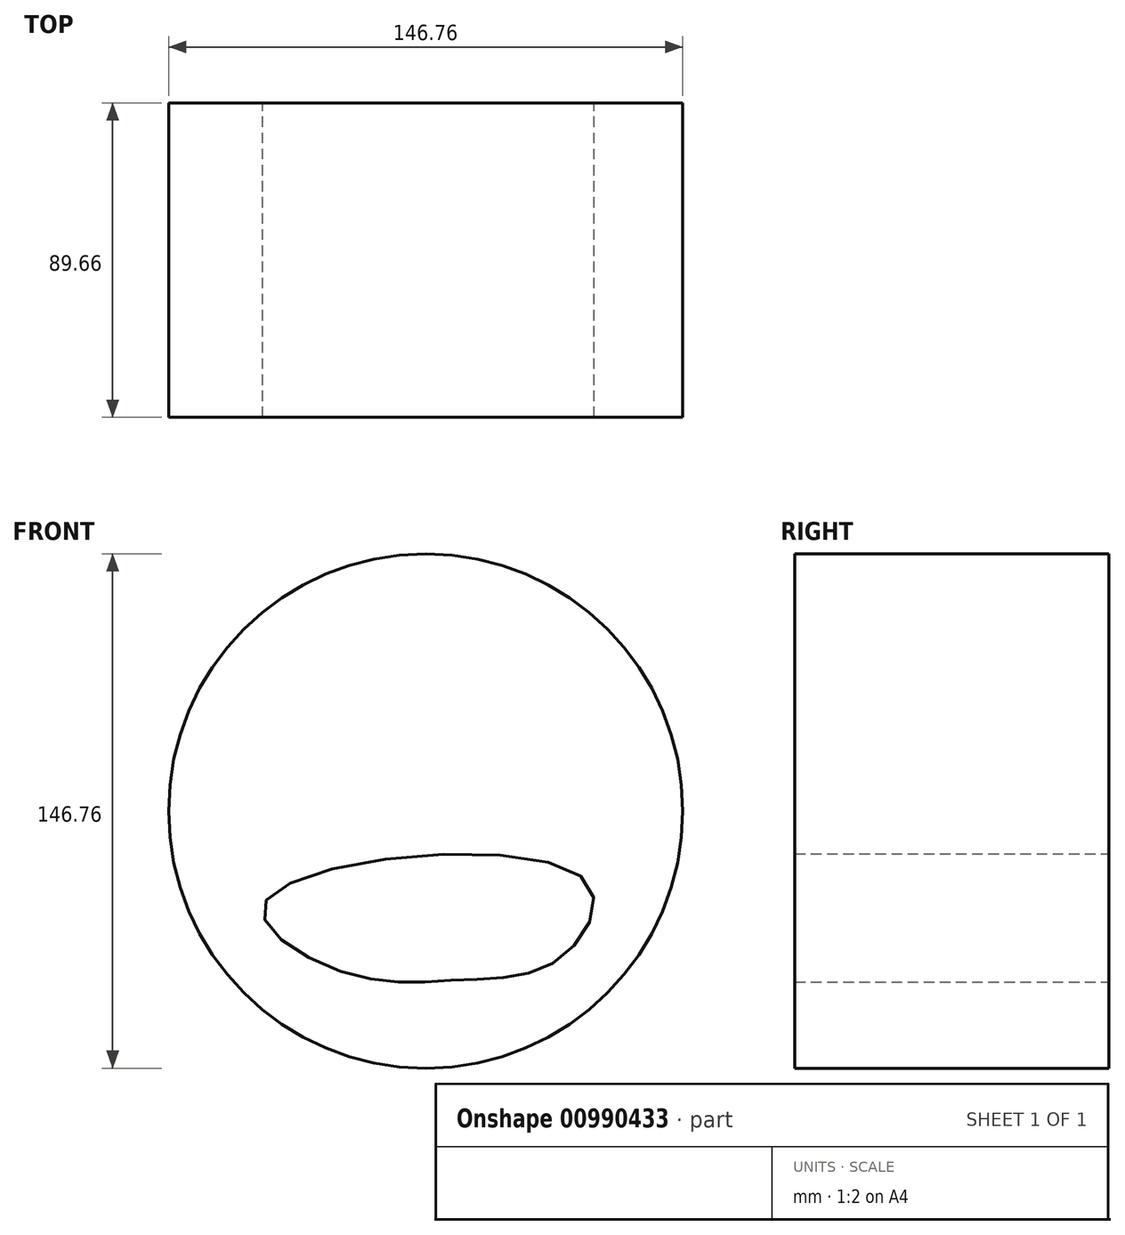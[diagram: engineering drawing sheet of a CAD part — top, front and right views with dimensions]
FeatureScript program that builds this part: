
annotation { "Feature Type Name" : "Feature", "Feature Type Description" : "" }
export const myFeature = defineFeature(function(context is Context, id is Id, definition is map)
    precondition{}
    {
        {
            var Q0;
            Q0=qCreatedBy(makeId("Front.planeOp"),FACE);
            var sketch = newSketch(context, id + "F0", { "sketchPlane" : qUnion([Q0])});
            skCircle(sketch, "E0", {"center": v(0, -1.7) * mm, "radius": 73.38 * mm});
            skSolve(sketch);
        }
        {
            var Q0;
            Q0=makeQuery(id+"F0.imprint","IMPRINT",FACE,{"disambiguationData":[TD([[makeQuery(id+"F0.imprint","IMPRINT",EDGE,{"derivedFrom":sQuery(id+"F0.wireOp",EDGE,"E0")}),1.0]])]});
            extrude(context, id + "F1", {"entities" : qUnion([Q0]), "depth" : 89.66 * mm, "offsetDistance" : 25.4 * mm});
        }
        {
            var Q0;
            Q0=makeQuery(id+"F1.opExtrude","CAP_FACE",FACE,{"disambiguationData":[OSD([sQuery(id+"F0.wireOp",EDGE,"E0")])],"isStart":false});
            var sketch = newSketch(context, id + "F2", { "sketchPlane" : qUnion([Q0])});
            skFitSpline(sketch, "E1", {"points": [v(-45.54, -27.2) * mm, v(-24.11, -47.54) * mm, v(9.65, -49.92) * mm, v(38.44, -43.64) * mm, v(44.5, -20.48) * mm, v(-45.54, -27.2) * mm]});
            skSolve(sketch);
        }
        {
            var Q0;
            Q0=makeQuery(id+"F2.imprint","IMPRINT",FACE,{"disambiguationData":[TD([[makeQuery(id+"F2.imprint","IMPRINT",EDGE,{"derivedFrom":sQuery(id+"F2.wireOp",EDGE,"E1")}),1.0]])]});
            extrude(context, id + "F3", {"entities" : qUnion([Q0]), "operationType" : NewBodyOperationType.REMOVE, "oppositeDirection" : true, "depth" : 343.66 * mm, "offsetDistance" : 25.4 * mm});
        }
    });
